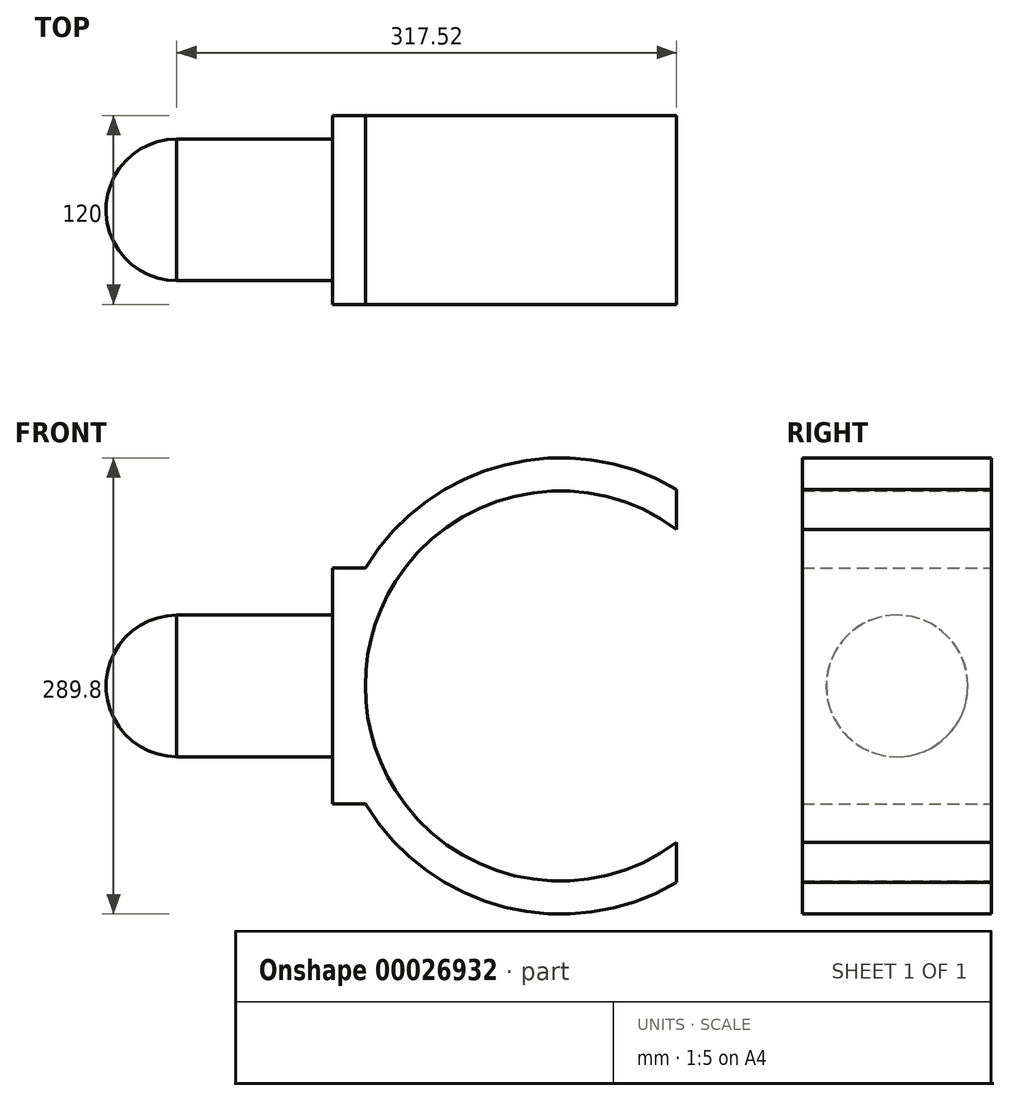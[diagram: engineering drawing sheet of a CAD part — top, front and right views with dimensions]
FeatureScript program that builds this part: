
annotation { "Feature Type Name" : "Feature", "Feature Type Description" : "" }
export const myFeature = defineFeature(function(context is Context, id is Id, definition is map)
    precondition{}
    {
        {
            var Q0;
            Q0=qCreatedBy(makeId("Front.planeOp"),FACE);
            var sketch = newSketch(context, id + "F0", { "sketchPlane" : qUnion([Q0])});
            skArc(sketch, "E0", {"start": v(94.9, -17.36) * mm, "mid": v(176.12, -65.06) * mm, "end": v(267.42, -41.87) * mm});
            skArc(sketch, "E1", {"start": v(69.9, -17.36) * mm, "mid": v(158.42, -82.85) * mm, "end": v(267.42, -67.2) * mm});
            skLineSegment(sketch, "E2", {"start": v(267.42, -67.2) * mm, "end": v(267.42, -41.87) * mm});
            skArc(sketch, "E3.trimOffspring", {"start": v(267.42, 157.16) * mm, "mid": v(176.12, 180.34) * mm, "end": v(94.9, 132.64) * mm});
            skArc(sketch, "E4.trimOffspring", {"start": v(267.42, 182.49) * mm, "mid": v(158.42, 198.14) * mm, "end": v(69.9, 132.64) * mm});
            skLineSegment(sketch, "E5.trimOffspring", {"start": v(267.42, 157.16) * mm, "end": v(267.42, 182.49) * mm});
            skArc(sketch, "E6", {"start": v(94.9, 132.64) * mm, "mid": v(69.7, 57.64) * mm, "end": v(94.9, -17.36) * mm});
            skLineSegment(sketch, "E7", {"start": v(48.97, 57.64) * mm, "end": v(-50.1, 57.64) * mm});
            skLineSegment(sketch, "E8", {"start": v(69.9, 132.64) * mm, "end": v(48.97, 132.64) * mm});
            skLineSegment(sketch, "E9", {"start": v(48.97, 57.64) * mm, "end": v(48.97, 132.64) * mm});
            skLineSegment(sketch, "E10", {"start": v(69.9, -17.36) * mm, "end": v(48.97, -17.36) * mm});
            skLineSegment(sketch, "E11", {"start": v(48.97, 57.64) * mm, "end": v(48.97, -17.36) * mm});
            skLineSegment(sketch, "E12", {"start": v(48.97, 57.64) * mm, "end": v(48.97, 12.64) * mm});
            skLineSegment(sketch, "E13", {"start": v(48.97, 12.64) * mm, "end": v(-50.1, 12.64) * mm});
            skLineSegment(sketch, "E14", {"start": v(-50.1, 12.64) * mm, "end": v(-50.1, 57.64) * mm});
            skSolve(sketch);
        }
        {
            var Q0;
            Q0=makeQuery(id+"F0.imprint","IMPRINT",FACE,{"disambiguationData":[TD([[makeQuery(id+"F0.imprint","IMPRINT",EDGE,{"derivedFrom":sQuery(id+"F0.wireOp",EDGE,"E0")}),-1.0]])]});
            extrude(context, id + "F1", {"entities" : qUnion([Q0]), "endBound" : BoundingType.SYMMETRIC, "depth" : 120 * mm});
        }
        {
            var Q0;
            Q0=makeQuery(id+"F0.imprint","IMPRINT",FACE,{"disambiguationData":[TD([[makeQuery(id+"F0.imprint","IMPRINT",EDGE,{"derivedFrom":sQuery(id+"F0.wireOp",EDGE,"E7")}),1.0]])]});
            var Q1;
            Q1=sQuery(id+"F0.wireOp",EDGE,"E7");
            revolve(context, id + "F2", {"operationType" : NewBodyOperationType.ADD, "entities" : qUnion([Q0]), "axis" : qUnion([Q1]), "revolveType" : RevolveType.FULL});
        }
        {
            var Q0;
            Q0=makeQuery(id+"F2.opRevolve","SWEPT_FACE",FACE,{"disambiguationData":[OSD([sQuery(id+"F0.wireOp",EDGE,"E14")])]});
            var sketch = newSketch(context, id + "F3", { "sketchPlane" : qUnion([Q0])});
            skLineSegment(sketch, "E15", {"start": v(0, 102.64) * mm, "end": v(0, 12.64) * mm});
            skArc(sketch, "E16", {"start": v(0, 12.64) * mm, "mid": v(44.9, 57.64) * mm, "end": v(0, 102.64) * mm});
            skSolve(sketch);
        }
        {
            var Q0;
            Q0=makeQuery(id+"F3.imprint","IMPRINT",FACE,{"disambiguationData":[TD([[makeQuery(id+"F3.imprint","IMPRINT",EDGE,{"derivedFrom":sQuery(id+"F3.wireOp",EDGE,"E15")}),1.0]])]});
            var Q1;
            Q1=sQuery(id+"F3.wireOp",EDGE,"E15");
            revolve(context, id + "F4", {"operationType" : NewBodyOperationType.ADD, "entities" : qUnion([Q0]), "axis" : qUnion([Q1]), "revolveType" : RevolveType.FULL});
        }
    });
